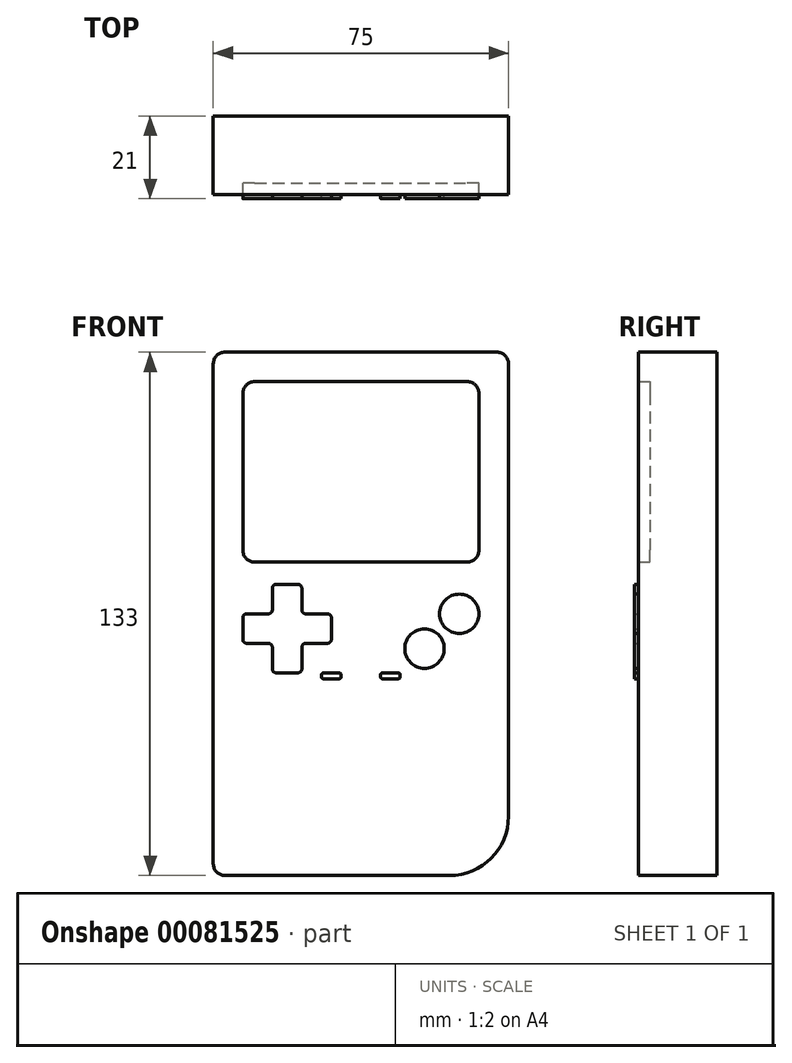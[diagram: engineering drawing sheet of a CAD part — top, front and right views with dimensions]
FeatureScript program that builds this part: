
annotation { "Feature Type Name" : "Feature", "Feature Type Description" : "" }
export const myFeature = defineFeature(function(context is Context, id is Id, definition is map)
    precondition{}
    {
        {
            var Q0;
            Q0=qCreatedBy(makeId("Front.planeOp"),FACE);
            var sketch = newSketch(context, id + "F0", { "sketchPlane" : qUnion([Q0])});
            skLineSegment(sketch, "E0.bottom", {"start": v(34.5, 66.5) * mm, "end": v(-34.5, 66.5) * mm});
            skLineSegment(sketch, "E0.top", {"start": v(22.5, -66.5) * mm, "end": v(-34.5, -66.5) * mm});
            skLineSegment(sketch, "E0.left", {"start": v(37.5, 63.5) * mm, "end": v(37.5, -51.5) * mm});
            skLineSegment(sketch, "E0.right", {"start": v(-37.5, 63.5) * mm, "end": v(-37.5, -63.5) * mm});
            skPoint(sketch, "E0.middle", {"position": v(0, 0) * mm});
            skPoint(sketch, "E1.visualSharp", {"position": v(-37.5, 66.5) * mm});
            skArc(sketch, "E1.filletArc", {"start": v(-34.5, 66.5) * mm, "mid": v(-36.62, 65.62) * mm, "end": v(-37.5, 63.5) * mm});
            skPoint(sketch, "E2.visualSharp", {"position": v(37.5, 66.5) * mm});
            skArc(sketch, "E2.filletArc", {"start": v(37.5, 63.5) * mm, "mid": v(36.62, 65.62) * mm, "end": v(34.5, 66.5) * mm});
            skPoint(sketch, "E3.visualSharp", {"position": v(-37.5, -66.5) * mm});
            skArc(sketch, "E3.filletArc", {"start": v(-37.5, -63.5) * mm, "mid": v(-36.62, -65.62) * mm, "end": v(-34.5, -66.5) * mm});
            skPoint(sketch, "E4.visualSharp", {"position": v(37.5, -66.5) * mm});
            skArc(sketch, "E4.filletArc", {"start": v(22.5, -66.5) * mm, "mid": v(33.1, -62.1) * mm, "end": v(37.5, -51.5) * mm});
            skLineSegment(sketch, "E5.bottom", {"start": v(-27, 59) * mm, "end": v(27, 59) * mm});
            skLineSegment(sketch, "E5.top", {"start": v(-27, 13.18) * mm, "end": v(27, 13.18) * mm});
            skLineSegment(sketch, "E5.left", {"start": v(-30, 56) * mm, "end": v(-30, 16.18) * mm});
            skLineSegment(sketch, "E5.right", {"start": v(30, 56) * mm, "end": v(30, 16.18) * mm});
            skLineSegment(sketch, "E6", {"start": v(0, 66.5) * mm, "end": v(0, 59) * mm, "construction": true});
            skLineSegment(sketch, "E7", {"start": v(30, 36.09) * mm, "end": v(37.5, 36.09) * mm, "construction": true});
            skLineSegment(sketch, "E8", {"start": v(-30, 36.09) * mm, "end": v(-37.5, 36.09) * mm, "construction": true});
            skPoint(sketch, "E9.visualSharp", {"position": v(-30, 13.18) * mm});
            skArc(sketch, "E9.filletArc", {"start": v(-30, 16.18) * mm, "mid": v(-29.12, 14.05) * mm, "end": v(-27, 13.18) * mm});
            skPoint(sketch, "E10.visualSharp", {"position": v(-30, 59) * mm});
            skArc(sketch, "E10.filletArc", {"start": v(-27, 59) * mm, "mid": v(-29.12, 58.12) * mm, "end": v(-30, 56) * mm});
            skPoint(sketch, "E11.visualSharp", {"position": v(30, 59) * mm});
            skArc(sketch, "E11.filletArc", {"start": v(30, 56) * mm, "mid": v(29.12, 58.12) * mm, "end": v(27, 59) * mm});
            skPoint(sketch, "E12.visualSharp", {"position": v(30, 13.18) * mm});
            skArc(sketch, "E12.filletArc", {"start": v(27, 13.18) * mm, "mid": v(29.12, 14.05) * mm, "end": v(30, 16.18) * mm});
            skSolve(sketch);
        }
        {
            var Q0;
            Q0=makeQuery(id+"F0.imprint","IMPRINT",FACE,{"disambiguationData":[TD([[makeQuery(id+"F0.imprint","IMPRINT",EDGE,{"derivedFrom":sQuery(id+"F0.wireOp",EDGE,"E0.bottom")}),1.0]])]});
            extrude(context, id + "F1", {"entities" : qUnion([Q0]), "depth" : 20 * mm});
        }
        {
            var Q0;
            Q0=makeQuery(id+"F0.imprint","IMPRINT",FACE,{"disambiguationData":[TD([[makeQuery(id+"F0.imprint","IMPRINT",EDGE,{"derivedFrom":sQuery(id+"F0.wireOp",EDGE,"E5.bottom")}),-1.0]])]});
            extrude(context, id + "F2", {"entities" : qUnion([Q0]), "operationType" : NewBodyOperationType.ADD, "depth" : 17 * mm});
        }
        {
            var Q0;
            Q0=makeQuery(id+"F1.opExtrude","CAP_FACE",FACE,{"disambiguationData":[OSD([sQuery(id+"F0.wireOp",EDGE,"E0.bottom"),sQuery(id+"F0.wireOp",EDGE,"E0.top"),sQuery(id+"F0.wireOp",EDGE,"E0.left"),sQuery(id+"F0.wireOp",EDGE,"E0.right"),sQuery(id+"F0.wireOp",EDGE,"E1.filletArc"),sQuery(id+"F0.wireOp",EDGE,"E2.filletArc"),sQuery(id+"F0.wireOp",EDGE,"E3.filletArc"),sQuery(id+"F0.wireOp",EDGE,"E4.filletArc"),sQuery(id+"F0.wireOp",EDGE,"E5.bottom"),sQuery(id+"F0.wireOp",EDGE,"E5.top"),sQuery(id+"F0.wireOp",EDGE,"E5.left"),sQuery(id+"F0.wireOp",EDGE,"E5.right")])],"isStart":false});
            var sketch = newSketch(context, id + "F3", { "sketchPlane" : qUnion([Q0])});
            skLineSegment(sketch, "E13", {"start": v(25, 0) * mm, "end": v(16.16, -8.84) * mm, "construction": true});
            skCircle(sketch, "E14", {"center": v(25, 0) * mm, "radius": 5 * mm});
            skCircle(sketch, "E15", {"center": v(16.16, -8.84) * mm, "radius": 5 * mm});
            skLineSegment(sketch, "E16.bottom", {"start": v(-21.5, 7.5) * mm, "end": v(-16, 7.5) * mm});
            skLineSegment(sketch, "E16.top", {"start": v(-21.5, -15) * mm, "end": v(-16, -15) * mm});
            skLineSegment(sketch, "E16.left", {"start": v(-22.5, 6.5) * mm, "end": v(-22.5, 1) * mm});
            skLineSegment(sketch, "E16.right", {"start": v(-15, 6.5) * mm, "end": v(-15, 1) * mm});
            skLineSegment(sketch, "E17.bottom", {"start": v(-29, 0) * mm, "end": v(-23.5, 0) * mm});
            skLineSegment(sketch, "E17.top", {"start": v(-29, -7.5) * mm, "end": v(-23.5, -7.5) * mm});
            skLineSegment(sketch, "E17.left", {"start": v(-30, -1) * mm, "end": v(-30, -6.5) * mm});
            skLineSegment(sketch, "E17.right", {"start": v(-7.5, -1) * mm, "end": v(-7.5, -6.5) * mm});
            skLineSegment(sketch, "E18", {"start": v(-18.75, 7.5) * mm, "end": v(-18.75, -3.75) * mm, "construction": true});
            skLineSegment(sketch, "E19", {"start": v(-30, -3.75) * mm, "end": v(-7.5, -3.75) * mm, "construction": true});
            skLineSegment(sketch, "E20", {"start": v(-18.75, -3.75) * mm, "end": v(-18.75, -15) * mm, "construction": true});
            skLineSegment(sketch, "E21.trimOffspring", {"start": v(-15, -8.5) * mm, "end": v(-15, -14) * mm});
            skLineSegment(sketch, "E22.trimOffspring", {"start": v(-14, -7.5) * mm, "end": v(-8.5, -7.5) * mm});
            skLineSegment(sketch, "E23.trimOffspring", {"start": v(-22.5, -8.5) * mm, "end": v(-22.5, -14) * mm});
            skLineSegment(sketch, "E24.trimOffspring", {"start": v(-14, 0) * mm, "end": v(-8.5, 0) * mm});
            skLineSegment(sketch, "E25.bottom", {"start": v(-9.5, -15) * mm, "end": v(-5.5, -15) * mm});
            skLineSegment(sketch, "E25.top", {"start": v(-9.5, -16.5) * mm, "end": v(-5.5, -16.5) * mm});
            skLineSegment(sketch, "E25.left", {"start": v(-10, -15.5) * mm, "end": v(-10, -16) * mm});
            skLineSegment(sketch, "E25.right", {"start": v(-5, -15.5) * mm, "end": v(-5, -16) * mm});
            skLineSegment(sketch, "E26.bottom", {"start": v(5.5, -15) * mm, "end": v(9.5, -15) * mm});
            skLineSegment(sketch, "E26.top", {"start": v(5.5, -16.5) * mm, "end": v(9.5, -16.5) * mm});
            skLineSegment(sketch, "E26.left", {"start": v(5, -15.5) * mm, "end": v(5, -16) * mm});
            skLineSegment(sketch, "E26.right", {"start": v(10, -15.5) * mm, "end": v(10, -16) * mm});
            skLineSegment(sketch, "E27", {"start": v(-5, -15) * mm, "end": v(0, -15) * mm, "construction": true});
            skLineSegment(sketch, "E28", {"start": v(0, -15) * mm, "end": v(5, -15) * mm, "construction": true});
            skLineSegment(sketch, "E29", {"start": v(0, 0) * mm, "end": v(0, -66.5) * mm});
            skPoint(sketch, "E30.visualSharp", {"position": v(-22.5, 7.5) * mm});
            skArc(sketch, "E30.filletArc", {"start": v(-21.5, 7.5) * mm, "mid": v(-22.2, 7.2) * mm, "end": v(-22.5, 6.5) * mm});
            skPoint(sketch, "E31.visualSharp", {"position": v(-15, 7.5) * mm});
            skArc(sketch, "E31.filletArc", {"start": v(-15, 6.5) * mm, "mid": v(-15.3, 7.2) * mm, "end": v(-16, 7.5) * mm});
            skPoint(sketch, "E32.visualSharp", {"position": v(-7.5, 0) * mm});
            skArc(sketch, "E32.filletArc", {"start": v(-7.5, -1) * mm, "mid": v(-7.8, -0.3) * mm, "end": v(-8.5, 0) * mm});
            skPoint(sketch, "E33.visualSharp", {"position": v(-7.5, -7.5) * mm});
            skArc(sketch, "E33.filletArc", {"start": v(-8.5, -7.5) * mm, "mid": v(-7.8, -7.2) * mm, "end": v(-7.5, -6.5) * mm});
            skPoint(sketch, "E34.visualSharp", {"position": v(-15, -7.5) * mm});
            skArc(sketch, "E34.filletArc", {"start": v(-14, -7.5) * mm, "mid": v(-14.7, -7.8) * mm, "end": v(-15, -8.5) * mm});
            skPoint(sketch, "E35.visualSharp", {"position": v(-15, 0) * mm});
            skArc(sketch, "E35.filletArc", {"start": v(-15, 1) * mm, "mid": v(-14.7, 0.3) * mm, "end": v(-14, 0) * mm});
            skPoint(sketch, "E36.visualSharp", {"position": v(-22.5, 0) * mm});
            skArc(sketch, "E36.filletArc", {"start": v(-23.5, 0) * mm, "mid": v(-22.8, 0.3) * mm, "end": v(-22.5, 1) * mm});
            skPoint(sketch, "E37.visualSharp", {"position": v(-30, 0) * mm});
            skArc(sketch, "E37.filletArc", {"start": v(-29, 0) * mm, "mid": v(-29.7, -0.3) * mm, "end": v(-30, -1) * mm});
            skPoint(sketch, "E38.visualSharp", {"position": v(-30, -7.5) * mm});
            skArc(sketch, "E38.filletArc", {"start": v(-30, -6.5) * mm, "mid": v(-29.7, -7.2) * mm, "end": v(-29, -7.5) * mm});
            skPoint(sketch, "E39.visualSharp", {"position": v(-22.5, -15) * mm});
            skArc(sketch, "E39.filletArc", {"start": v(-22.5, -14) * mm, "mid": v(-22.2, -14.7) * mm, "end": v(-21.5, -15) * mm});
            skPoint(sketch, "E40.visualSharp", {"position": v(-15, -15) * mm});
            skArc(sketch, "E40.filletArc", {"start": v(-16, -15) * mm, "mid": v(-15.3, -14.7) * mm, "end": v(-15, -14) * mm});
            skPoint(sketch, "E41.visualSharp", {"position": v(-22.5, -7.5) * mm});
            skArc(sketch, "E41.filletArc", {"start": v(-22.5, -8.5) * mm, "mid": v(-22.8, -7.8) * mm, "end": v(-23.5, -7.5) * mm});
            skPoint(sketch, "E42.visualSharp", {"position": v(-5, -15) * mm});
            skArc(sketch, "E42.filletArc", {"start": v(-5, -15.5) * mm, "mid": v(-5.15, -15.15) * mm, "end": v(-5.5, -15) * mm});
            skPoint(sketch, "E43.visualSharp", {"position": v(-10, -15) * mm});
            skArc(sketch, "E43.filletArc", {"start": v(-9.5, -15) * mm, "mid": v(-9.85, -15.15) * mm, "end": v(-10, -15.5) * mm});
            skPoint(sketch, "E44.visualSharp", {"position": v(-10, -16.5) * mm});
            skArc(sketch, "E44.filletArc", {"start": v(-10, -16) * mm, "mid": v(-9.85, -16.35) * mm, "end": v(-9.5, -16.5) * mm});
            skPoint(sketch, "E45.visualSharp", {"position": v(-5, -16.5) * mm});
            skArc(sketch, "E45.filletArc", {"start": v(-5.5, -16.5) * mm, "mid": v(-5.15, -16.35) * mm, "end": v(-5, -16) * mm});
            skPoint(sketch, "E46.visualSharp", {"position": v(5, -15) * mm});
            skArc(sketch, "E46.filletArc", {"start": v(5.5, -15) * mm, "mid": v(5.15, -15.15) * mm, "end": v(5, -15.5) * mm});
            skPoint(sketch, "E47.visualSharp", {"position": v(10, -15) * mm});
            skArc(sketch, "E47.filletArc", {"start": v(10, -15.5) * mm, "mid": v(9.85, -15.15) * mm, "end": v(9.5, -15) * mm});
            skPoint(sketch, "E48.visualSharp", {"position": v(10, -16.5) * mm});
            skArc(sketch, "E48.filletArc", {"start": v(9.5, -16.5) * mm, "mid": v(9.85, -16.35) * mm, "end": v(10, -16) * mm});
            skPoint(sketch, "E49.visualSharp", {"position": v(5, -16.5) * mm});
            skArc(sketch, "E49.filletArc", {"start": v(5, -16) * mm, "mid": v(5.15, -16.35) * mm, "end": v(5.5, -16.5) * mm});
            skSolve(sketch);
        }
        {
            var Q0;
            Q0=makeQuery(id+"F3.imprint","IMPRINT",FACE,{"disambiguationData":[TD([[makeQuery(id+"F3.imprint","IMPRINT",EDGE,{"derivedFrom":sQuery(id+"F3.wireOp",EDGE,"E16.bottom")}),-1.0]])]});
            var Q1;
            Q1=makeQuery(id+"F3.imprint","IMPRINT",FACE,{"disambiguationData":[TD([[makeQuery(id+"F3.imprint","IMPRINT",EDGE,{"derivedFrom":sQuery(id+"F3.wireOp",EDGE,"E25.bottom")}),-1.0]])]});
            var Q2;
            Q2=makeQuery(id+"F3.imprint","IMPRINT",FACE,{"disambiguationData":[TD([[makeQuery(id+"F3.imprint","IMPRINT",EDGE,{"derivedFrom":sQuery(id+"F3.wireOp",EDGE,"E26.bottom")}),-1.0]])]});
            var Q3;
            Q3=makeQuery(id+"F3.imprint","IMPRINT",FACE,{"disambiguationData":[TD([[makeQuery(id+"F3.imprint","IMPRINT",EDGE,{"derivedFrom":sQuery(id+"F3.wireOp",EDGE,"E15")}),1.0]])]});
            var Q4;
            Q4=makeQuery(id+"F3.imprint","IMPRINT",FACE,{"disambiguationData":[TD([[makeQuery(id+"F3.imprint","IMPRINT",EDGE,{"derivedFrom":sQuery(id+"F3.wireOp",EDGE,"E14")}),1.0]])]});
            extrude(context, id + "F4", {"entities" : qUnion([Q0, Q1, Q2, Q3, Q4]), "depth" : 1 * mm});
        }
    });
